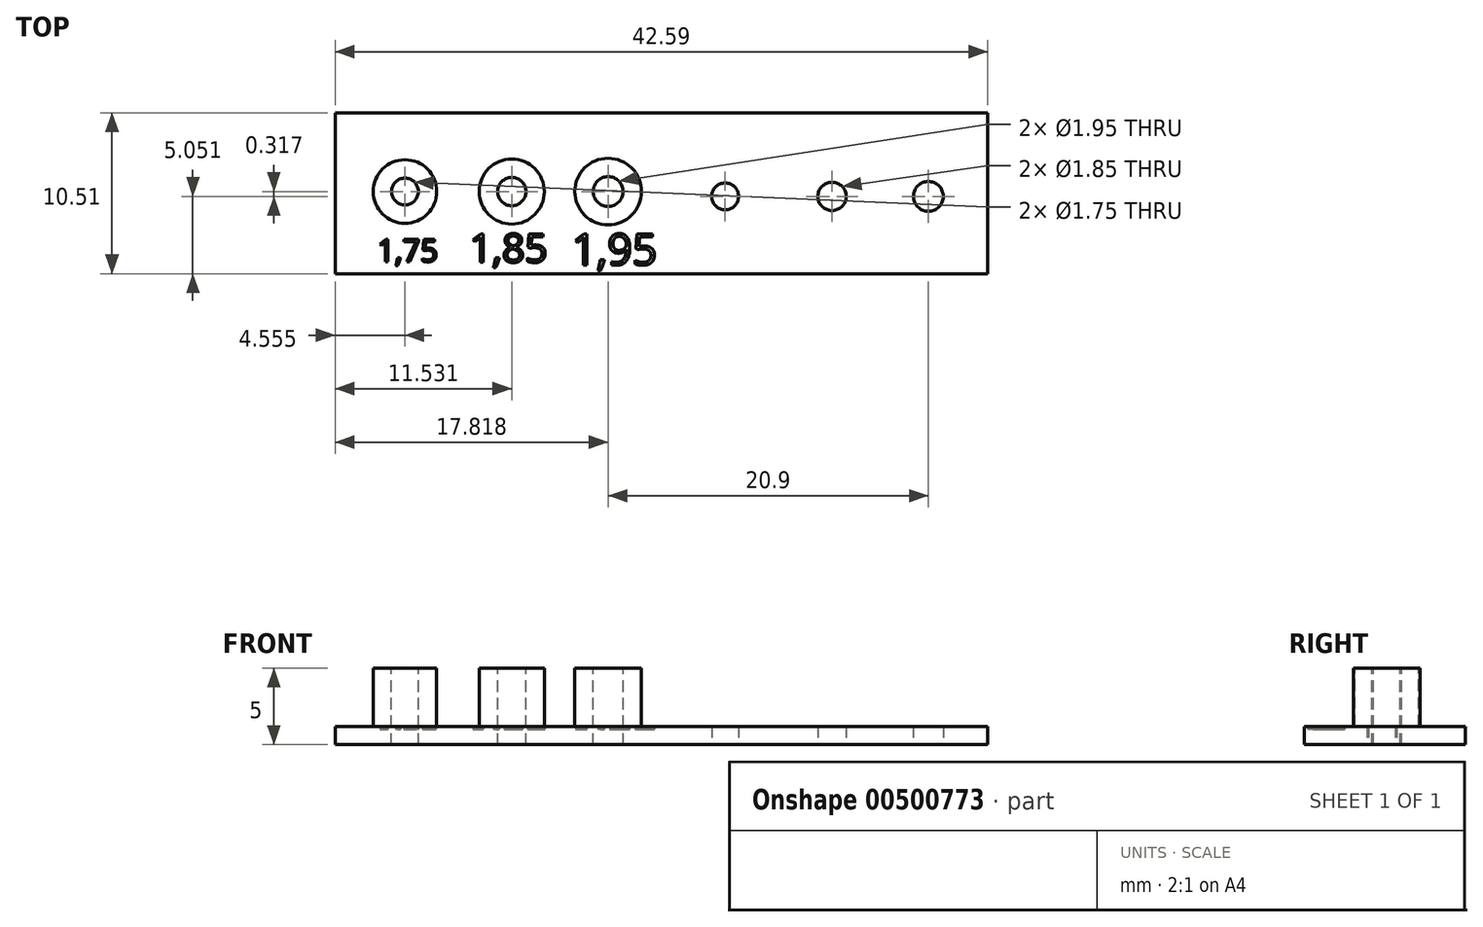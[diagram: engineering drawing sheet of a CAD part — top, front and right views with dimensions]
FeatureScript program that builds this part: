
annotation { "Feature Type Name" : "Feature", "Feature Type Description" : "" }
export const myFeature = defineFeature(function(context is Context, id is Id, definition is map)
    precondition{}
    {
        {
            var Q0;
            Q0=qCreatedBy(makeId("Top.planeOp"),FACE);
            var sketch = newSketch(context, id + "F0", { "sketchPlane" : qUnion([Q0])});
            skLineSegment(sketch, "E0.bottom", {"start": v(-75.68, 20.26) * mm, "end": v(-33.1, 20.26) * mm});
            skLineSegment(sketch, "E0.top", {"start": v(-75.68, 9.75) * mm, "end": v(-33.1, 9.75) * mm});
            skLineSegment(sketch, "E0.left", {"start": v(-75.68, 20.26) * mm, "end": v(-75.68, 9.75) * mm});
            skLineSegment(sketch, "E0.right", {"start": v(-33.1, 20.26) * mm, "end": v(-33.1, 9.75) * mm});
            skSolve(sketch);
        }
        {
            var Q0;
            Q0=makeQuery(id+"F0.imprint","IMPRINT",FACE,{"disambiguationData":[TD([[makeQuery(id+"F0.imprint","IMPRINT",EDGE,{"derivedFrom":sQuery(id+"F0.wireOp",EDGE,"E0.bottom")}),-1.0]])]});
            extrude(context, id + "F1", {"entities" : qUnion([Q0]), "depth" : 5 * mm});
        }
        {
            var Q0;
            Q0=makeQuery(id+"F1.opExtrude","CAP_FACE",FACE,{"disambiguationData":[OSD([sQuery(id+"F0.wireOp",EDGE,"E0.bottom"),sQuery(id+"F0.wireOp",EDGE,"E0.top"),sQuery(id+"F0.wireOp",EDGE,"E0.left"),sQuery(id+"F0.wireOp",EDGE,"E0.right")])],"isStart":false});
            var sketch = newSketch(context, id + "F2", { "sketchPlane" : qUnion([Q0])});
            skCircle(sketch, "E1", {"center": v(-71.13, 15.12) * mm, "radius": 0.88 * mm});
            skCircle(sketch, "E2", {"center": v(-64.15, 15.12) * mm, "radius": 0.93 * mm});
            skCircle(sketch, "E3", {"center": v(-57.86, 15.12) * mm, "radius": 0.97 * mm});
            skSolve(sketch);
        }
        {
            var Q0;
            Q0 = qSketchRegion(id + "F2", true);
            extrude(context, id + "F3", {"entities" : qUnion([Q0]), "operationType" : NewBodyOperationType.REMOVE, "oppositeDirection" : true, "depth" : 25 * mm});
        }
        {
            var Q0;
            Q0=makeQuery(id+"F1.opExtrude","CAP_FACE",FACE,{"disambiguationData":[OSD([sQuery(id+"F0.wireOp",EDGE,"E0.bottom"),sQuery(id+"F0.wireOp",EDGE,"E0.top"),sQuery(id+"F0.wireOp",EDGE,"E0.left"),sQuery(id+"F0.wireOp",EDGE,"E0.right")])],"isStart":false});
            var Q1;
            Q1=makeQuery(id+"F1.opExtrude","SWEPT_FACE",FACE,{"disambiguationData":[OSD([sQuery(id+"F0.wireOp",EDGE,"E0.top")])]});
            var Q2;
            Q2=makeQuery(id+"F1.opExtrude","SWEPT_FACE",FACE,{"disambiguationData":[OSD([sQuery(id+"F0.wireOp",EDGE,"E0.right")])]});
            var Q3;
            Q3=makeQuery(id+"F1.opExtrude","SWEPT_FACE",FACE,{"disambiguationData":[OSD([sQuery(id+"F0.wireOp",EDGE,"E0.bottom")])]});
            var Q4;
            Q4=makeQuery(id+"F1.opExtrude","SWEPT_FACE",FACE,{"disambiguationData":[OSD([sQuery(id+"F0.wireOp",EDGE,"E0.left")])]});
            shell(context, id + "F4", {"entities" : qUnion([Q0, Q1, Q2, Q3, Q4]), "thickness" : 1.2 * mm});
        }
        {
            var Q0;
            Q0=qCreatedBy(makeId("Top.planeOp"),FACE);
            var sketch = newSketch(context, id + "F5", { "sketchPlane" : qUnion([Q0])});
            skCircle(sketch, "E4", {"center": v(-50.23, 14.8) * mm, "radius": 0.88 * mm});
            skCircle(sketch, "E5", {"center": v(-43.25, 14.8) * mm, "radius": 0.93 * mm});
            skCircle(sketch, "E6", {"center": v(-36.96, 14.8) * mm, "radius": 0.97 * mm});
            skSolve(sketch);
        }
        {
            var Q0;
            Q0 = qSketchRegion(id + "F5", true);
            extrude(context, id + "F6", {"entities" : qUnion([Q0]), "operationType" : NewBodyOperationType.REMOVE, "depth" : 25 * mm});
        }
        {
            var Q0;
            Q0=qCreatedBy(makeId("Top.planeOp"),FACE);
            var sketch = newSketch(context, id + "F7", { "sketchPlane" : qUnion([Q0])});
            skText(sketch, "E7", { "text": "1,75", "fontName": "OpenSans-Regular.ttf"});
            skText(sketch, "E8", { "text": "1,75", "fontName": "OpenSans-Regular.ttf"});
            skText(sketch, "E9", { "text": "1,75", "fontName": "OpenSans-Regular.ttf"});
            skText(sketch, "E10", { "text": "1,75", "fontName": "OpenSans-Regular.ttf"});
            skText(sketch, "E11", { "text": "1,85", "fontName": "OpenSans-Regular.ttf"});
            skText(sketch, "E12", { "text": "1,95", "fontName": "OpenSans-Regular.ttf"});
            const initialGuessF7  = {"E7": [-0.07294, 0.01054, 1, 0, 0.00146], "E8": [-0.13655, 0.02303, 1, 0, 0.00146], "E9": [-0.1411, 0.02152, 1, 0, 0.00146], "E10": [-0.20377, 0.03392, 1, 0, 0.00146], "E11": [-0.06691, 0.0105, 1, 0, 0.00187], "E12": [-0.06023, 0.01033, 1, 0, 0.00204]};
            skSetInitialGuess(sketch, initialGuessF7);
            skSolve(sketch);
        }
        {
            var Q0;
            Q0 = qSketchRegion(id + "F7", true);
            extrude(context, id + "F8", {"entities" : qUnion([Q0]), "operationType" : NewBodyOperationType.REMOVE, "depth" : 1.5 * mm, "hasSecondDirection" : true, "secondDirectionOppositeDirection" : false, "secondDirectionDepth" : 1 * mm});
        }
    });
